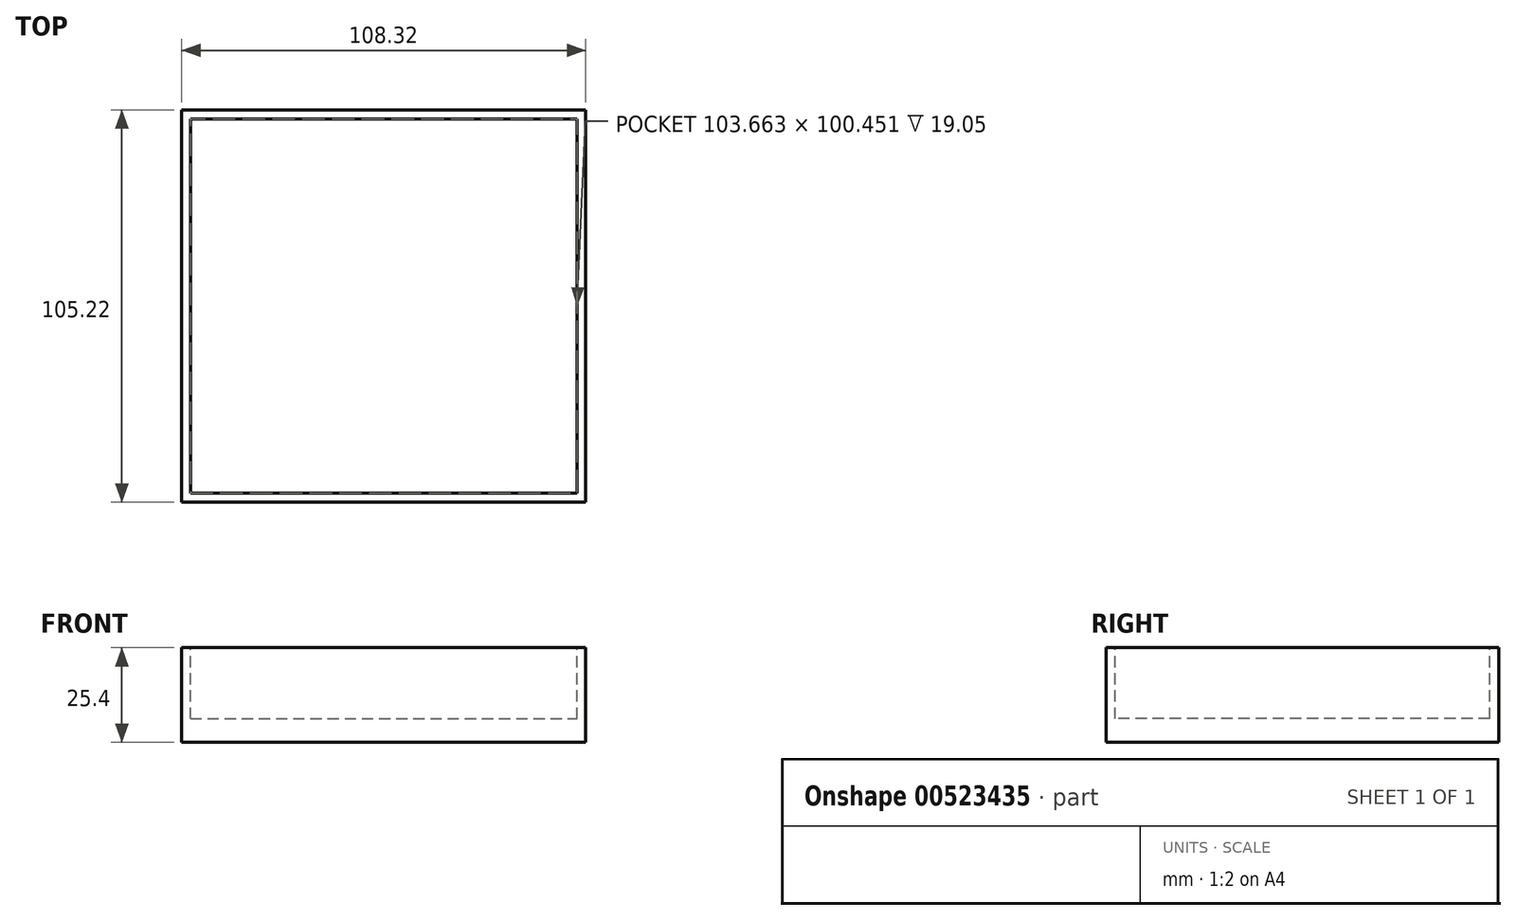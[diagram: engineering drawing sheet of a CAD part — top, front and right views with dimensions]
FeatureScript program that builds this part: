
annotation { "Feature Type Name" : "Feature", "Feature Type Description" : "" }
export const myFeature = defineFeature(function(context is Context, id is Id, definition is map)
    precondition{}
    {
        {
            var Q0;
            Q0=qCreatedBy(makeId("Top.planeOp"),FACE);
            var sketch = newSketch(context, id + "F0", { "sketchPlane" : qUnion([Q0])});
            skLineSegment(sketch, "E0.bottom", {"start": v(-54.16, 52.61) * mm, "end": v(54.16, 52.61) * mm});
            skLineSegment(sketch, "E0.top", {"start": v(-54.16, -52.61) * mm, "end": v(54.16, -52.61) * mm});
            skLineSegment(sketch, "E0.left", {"start": v(-54.16, 52.61) * mm, "end": v(-54.16, -52.61) * mm});
            skLineSegment(sketch, "E0.right", {"start": v(54.16, 52.61) * mm, "end": v(54.16, -52.61) * mm});
            skSolve(sketch);
        }
        {
            var Q0;
            Q0=makeQuery(id+"F0.imprint","IMPRINT",FACE,{"disambiguationData":[TD([[makeQuery(id+"F0.imprint","IMPRINT",EDGE,{"derivedFrom":sQuery(id+"F0.wireOp",EDGE,"E0.bottom")}),-1.0]])]});
            var Q1;
            Q1=sQuery(id+"F0.wireOp",EDGE,"E0.bottom");
            var Q2;
            Q2=sQuery(id+"F0.wireOp",EDGE,"E0.top");
            var Q3;
            Q3=sQuery(id+"F0.wireOp",EDGE,"E0.left");
            var Q4;
            Q4=sQuery(id+"F0.wireOp",EDGE,"E0.right");
            extrude(context, id + "F1", {"entities" : qUnion([Q0]), "surfaceEntities" : qUnion([Q1, Q2, Q3, Q4]), "depth" : 25.4 * mm, "offsetDistance" : 25.4 * mm});
        }
        {
            var Q0;
            Q0=makeQuery(id+"F1.opExtrude","CAP_FACE",FACE,{"disambiguationData":[OSD([sQuery(id+"F0.wireOp",EDGE,"E0.bottom"),sQuery(id+"F0.wireOp",EDGE,"E0.top"),sQuery(id+"F0.wireOp",EDGE,"E0.left"),sQuery(id+"F0.wireOp",EDGE,"E0.right")])],"isStart":false});
            var sketch = newSketch(context, id + "F2", { "sketchPlane" : qUnion([Q0])});
            skLineSegment(sketch, "E1.bottom", {"start": v(-51.83, 50.23) * mm, "end": v(51.83, 50.23) * mm});
            skLineSegment(sketch, "E1.top", {"start": v(-51.83, -50.23) * mm, "end": v(51.83, -50.23) * mm});
            skLineSegment(sketch, "E1.left", {"start": v(-51.83, 50.23) * mm, "end": v(-51.83, -50.23) * mm});
            skLineSegment(sketch, "E1.right", {"start": v(51.83, 50.23) * mm, "end": v(51.83, -50.23) * mm});
            skSolve(sketch);
        }
        {
            var Q0;
            Q0=makeQuery(id+"F2.imprint","IMPRINT",FACE,{"disambiguationData":[TD([[makeQuery(id+"F2.imprint","IMPRINT",EDGE,{"derivedFrom":sQuery(id+"F2.wireOp",EDGE,"E1.bottom")}),-1.0]])]});
            var Q1;
            Q1=sQuery(id+"F2.wireOp",EDGE,"E1.bottom");
            var Q2;
            Q2=sQuery(id+"F2.wireOp",EDGE,"E1.top");
            var Q3;
            Q3=sQuery(id+"F2.wireOp",EDGE,"E1.left");
            var Q4;
            Q4=sQuery(id+"F2.wireOp",EDGE,"E1.right");
            extrude(context, id + "F3", {"entities" : qUnion([Q0]), "operationType" : NewBodyOperationType.REMOVE, "surfaceEntities" : qUnion([Q1, Q2, Q3, Q4]), "oppositeDirection" : true, "depth" : 19.05 * mm, "offsetDistance" : 25.4 * mm});
        }
    });
